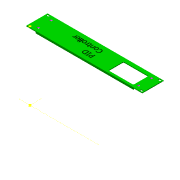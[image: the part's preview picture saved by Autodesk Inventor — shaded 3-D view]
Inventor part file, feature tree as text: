
AUTODESK INVENTOR PART (.ipt)
format: ipt  version: 2016 SP2 (Build 200236200, 236)  size: 183,808 bytes
history: native  units: mm
features: sketch x3, extrude x1, fillet x1, reference x1
ambient origin geometry x8: Origin, YZ Plane, XZ Plane, XY Plane, X Axis, Y Axis, Z Axis, Center Point
bodies: Solid1 (feature_tree)
feature tree (6):
  sketch  "Sketch1"  dims[d0=3.0mm d1=0.0mm d2=0.0mm d3=4.0mm]
  sketch  "Sketch2"
  extrude  "Extrusion1"  TaperAngle=0.0deg  [1 undecoded]
  fillet  "Fillet1"  Radius=4.0mm
  sketch  "Sketch3"
  reference  "Reference1"
note: 1 required parameter value undecoded (feature->parameter linkage not recoverable at this tier; creation-order binding heuristic only, values carry confidence <= 0.55)
